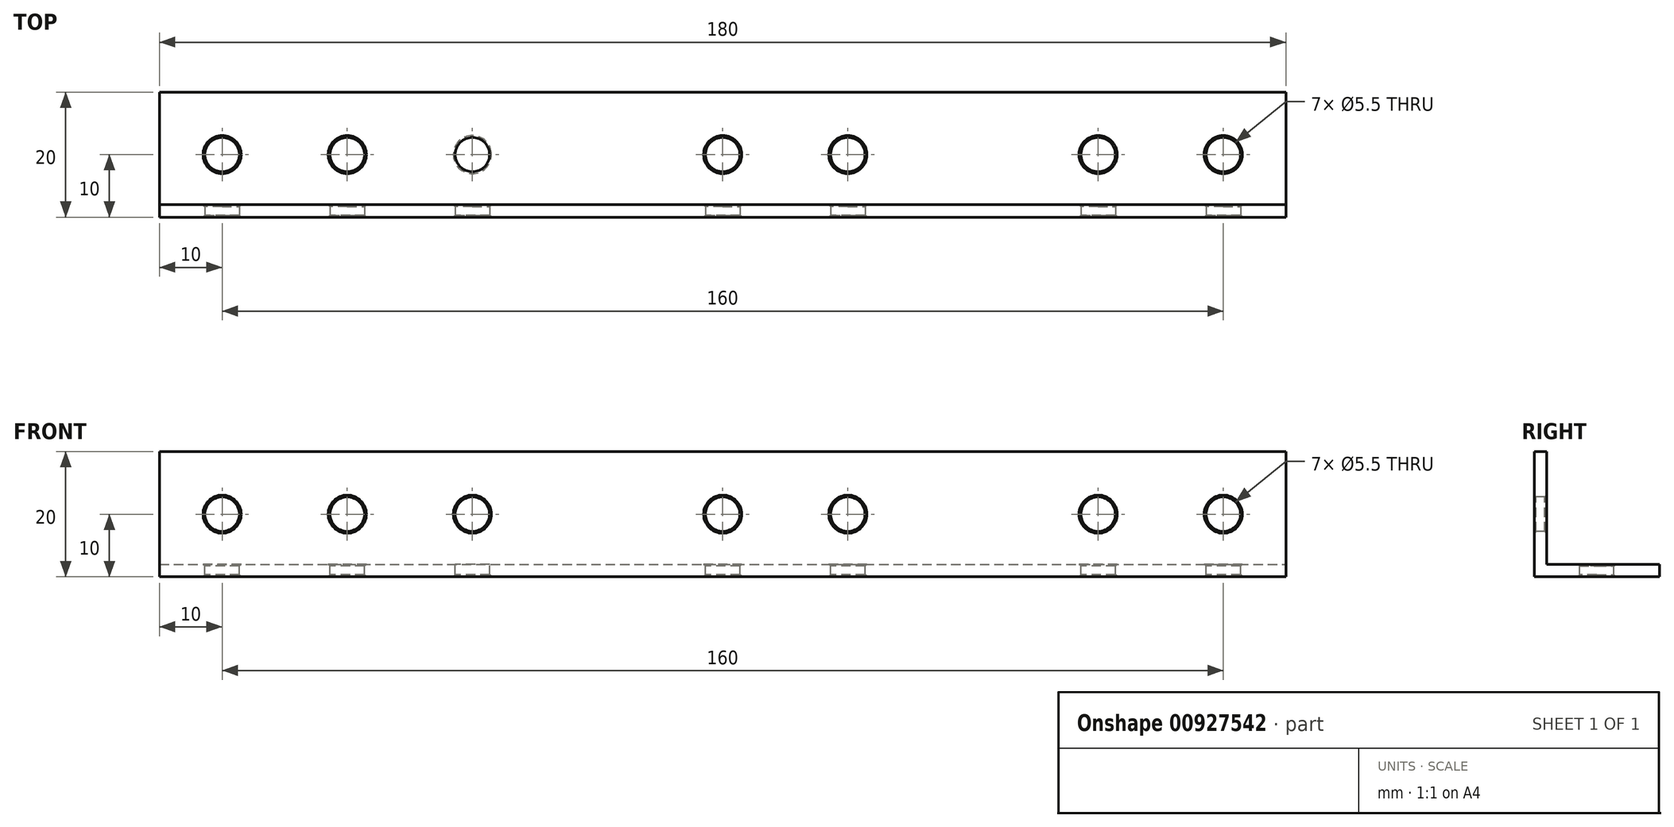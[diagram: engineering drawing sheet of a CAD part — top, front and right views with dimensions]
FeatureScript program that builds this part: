
annotation { "Feature Type Name" : "Feature", "Feature Type Description" : "" }
export const myFeature = defineFeature(function(context is Context, id is Id, definition is map)
    precondition{}
    {
        {
            var Q0;
            Q0=qCreatedBy(makeId("Right.planeOp"),FACE);
            var sketch = newSketch(context, id + "F0", { "sketchPlane" : qUnion([Q0])});
            skLineSegment(sketch, "E0", {"start": v(0, 0) * mm, "end": v(20, 0) * mm});
            skLineSegment(sketch, "E1", {"start": v(20, 0) * mm, "end": v(20, 2) * mm});
            skLineSegment(sketch, "E2", {"start": v(20, 2) * mm, "end": v(2, 2) * mm});
            skLineSegment(sketch, "E3", {"start": v(2, 2) * mm, "end": v(2, 20) * mm});
            skLineSegment(sketch, "E4", {"start": v(2, 20) * mm, "end": v(0, 20) * mm});
            skLineSegment(sketch, "E5", {"start": v(0, 20) * mm, "end": v(0, 0) * mm});
            skSolve(sketch);
        }
        {
            var Q0;
            Q0 = qSketchRegion(id + "F0", true);
            extrude(context, id + "F1", {"entities" : qUnion([Q0]), "oppositeDirection" : true, "depth" : 180 * mm, "offsetDistance" : 25 * mm});
        }
        {
            var Q0;
            Q0=makeQuery(id+"F1.opExtrude","SWEPT_FACE",FACE,{"disambiguationData":[OSD([sQuery(id+"F0.wireOp",EDGE,"E2")])]});
            var sketch = newSketch(context, id + "F2", { "sketchPlane" : qUnion([Q0])});
            skLineSegment(sketch, "E6", {"start": v(-203.4, 10) * mm, "end": v(31.76, 10) * mm, "construction": true});
            skLineSegment(sketch, "E7", {"start": v(-170, 30.5) * mm, "end": v(-170, -11.88) * mm, "construction": true});
            skLineSegment(sketch, "E8", {"start": v(-10, 33.17) * mm, "end": v(-10, -8.91) * mm, "construction": true});
            skCircle(sketch, "E9", {"center": v(-10, 10) * mm, "radius": 2.75 * mm});
            skLineSegment(sketch, "E10", {"start": v(-30, 32.56) * mm, "end": v(-30, -5.19) * mm, "construction": true});
            skLineSegment(sketch, "E11", {"start": v(-70, 34.23) * mm, "end": v(-70, -5.26) * mm, "construction": true});
            skLineSegment(sketch, "E12", {"start": v(-90, 33.62) * mm, "end": v(-90, -7.47) * mm, "construction": true});
            skLineSegment(sketch, "E13", {"start": v(-150, 31.7) * mm, "end": v(-150, -10.96) * mm, "construction": true});
            skCircle(sketch, "E14", {"center": v(-170, 10) * mm, "radius": 2.75 * mm});
            skCircle(sketch, "E15", {"center": v(-150, 10) * mm, "radius": 2.75 * mm});
            skCircle(sketch, "E16", {"center": v(-90, 10) * mm, "radius": 2.75 * mm});
            skCircle(sketch, "E17", {"center": v(-70, 10) * mm, "radius": 2.75 * mm});
            skCircle(sketch, "E18", {"center": v(-30, 10) * mm, "radius": 2.75 * mm});
            skLineSegment(sketch, "E19", {"start": v(-130, 30.56) * mm, "end": v(-130, -11.52) * mm, "construction": true});
            skCircle(sketch, "E20", {"center": v(-130, 10) * mm, "radius": 2.75 * mm});
            skSolve(sketch);
        }
        {
            var Q0;
            Q0 = qSketchRegion(id + "F2", true);
            extrude(context, id + "F3", {"entities" : qUnion([Q0]), "operationType" : NewBodyOperationType.REMOVE, "endBound" : BoundingType.THROUGH_ALL, "oppositeDirection" : true, "depth" : 25 * mm, "offsetDistance" : 25 * mm});
        }
        {
            var Q0;
            Q0=makeQuery(id+"F1.opExtrude","SWEPT_FACE",FACE,{"disambiguationData":[OSD([sQuery(id+"F0.wireOp",EDGE,"E5")])]});
            var sketch = newSketch(context, id + "F4", { "sketchPlane" : qUnion([Q0])});
            skLineSegment(sketch, "E21", {"start": v(-271.94, 10) * mm, "end": v(100.76, 10) * mm, "construction": true});
            skLineSegment(sketch, "E22", {"start": v(-10, 35.8) * mm, "end": v(-10, -12.15) * mm, "construction": true});
            skLineSegment(sketch, "E23", {"start": v(-30, 36.04) * mm, "end": v(-30, -10.38) * mm, "construction": true});
            skLineSegment(sketch, "E24", {"start": v(-70, 30.56) * mm, "end": v(-70, -11.43) * mm, "construction": true});
            skLineSegment(sketch, "E25", {"start": v(-90, 30.4) * mm, "end": v(-90, -9.66) * mm, "construction": true});
            skLineSegment(sketch, "E26", {"start": v(-150, 31.2) * mm, "end": v(-150, -10.06) * mm, "construction": true});
            skLineSegment(sketch, "E27", {"start": v(-170, 31.04) * mm, "end": v(-170, -9.17) * mm, "construction": true});
            skCircle(sketch, "E28", {"center": v(-170, 10) * mm, "radius": 2.75 * mm});
            skCircle(sketch, "E29", {"center": v(-150, 10) * mm, "radius": 2.75 * mm});
            skCircle(sketch, "E30", {"center": v(-90, 10) * mm, "radius": 2.75 * mm});
            skCircle(sketch, "E31", {"center": v(-70, 10) * mm, "radius": 2.75 * mm});
            skCircle(sketch, "E32", {"center": v(-30, 10) * mm, "radius": 2.75 * mm});
            skCircle(sketch, "E33", {"center": v(-10, 10) * mm, "radius": 2.75 * mm});
            skLineSegment(sketch, "E34", {"start": v(-130, 33.32) * mm, "end": v(-130, -20.97) * mm, "construction": true});
            skCircle(sketch, "E35", {"center": v(-130, 10) * mm, "radius": 2.75 * mm});
            skSolve(sketch);
        }
        {
            var Q0;
            Q0 = qSketchRegion(id + "F4", true);
            extrude(context, id + "F5", {"entities" : qUnion([Q0]), "operationType" : NewBodyOperationType.REMOVE, "endBound" : BoundingType.THROUGH_ALL, "oppositeDirection" : true, "depth" : 25 * mm, "offsetDistance" : 25 * mm});
        }
        {
            var Q0;
            Q0=makeQuery(id+"F3.boolean.opBoolean","COPY",FACE,{"derivedFrom":makeQuery(id+"F3.opExtrude","SWEPT_FACE",FACE,{"disambiguationData":[OSD([sQuery(id+"F2.wireOp",EDGE,"E14")])]})});
            var Q1;
            Q1=makeQuery(id+"F3.boolean.opBoolean","COPY",FACE,{"derivedFrom":makeQuery(id+"F3.opExtrude","SWEPT_FACE",FACE,{"disambiguationData":[OSD([sQuery(id+"F2.wireOp",EDGE,"E15")])]})});
            var Q2;
            Q2=makeQuery(id+"F3.boolean.opBoolean","COPY",FACE,{"derivedFrom":makeQuery(id+"F3.opExtrude","SWEPT_FACE",FACE,{"disambiguationData":[OSD([sQuery(id+"F2.wireOp",EDGE,"E16")])]})});
            var Q3;
            Q3=makeQuery(id+"F3.boolean.opBoolean","COPY",FACE,{"derivedFrom":makeQuery(id+"F3.opExtrude","SWEPT_FACE",FACE,{"disambiguationData":[OSD([sQuery(id+"F2.wireOp",EDGE,"E17")])]})});
            var Q4;
            Q4=makeQuery(id+"F3.boolean.opBoolean","COPY",FACE,{"derivedFrom":makeQuery(id+"F3.opExtrude","SWEPT_FACE",FACE,{"disambiguationData":[OSD([sQuery(id+"F2.wireOp",EDGE,"jkiNYSs5-8us3-oUFR-jLsB-93ToUElgCjty")])]})});
            var Q5;
            Q5=makeQuery(id+"F3.boolean.opBoolean","COPY",FACE,{"derivedFrom":makeQuery(id+"F3.opExtrude","SWEPT_FACE",FACE,{"disambiguationData":[OSD([sQuery(id+"F2.wireOp",EDGE,"E18")])]})});
            var Q6;
            Q6=makeQuery(id+"F3.boolean.opBoolean","COPY",FACE,{"derivedFrom":makeQuery(id+"F3.opExtrude","SWEPT_FACE",FACE,{"disambiguationData":[OSD([sQuery(id+"F2.wireOp",EDGE,"E9")])]})});
            var Q7;
            Q7=makeQuery(id+"F5.boolean.opBoolean","COPY",FACE,{"derivedFrom":makeQuery(id+"F5.opExtrude","SWEPT_FACE",FACE,{"disambiguationData":[OSD([sQuery(id+"F4.wireOp",EDGE,"E33")])]})});
            var Q8;
            Q8=makeQuery(id+"F5.boolean.opBoolean","COPY",FACE,{"derivedFrom":makeQuery(id+"F5.opExtrude","SWEPT_FACE",FACE,{"disambiguationData":[OSD([sQuery(id+"F4.wireOp",EDGE,"E32")])]})});
            var Q9;
            Q9=makeQuery(id+"F5.boolean.opBoolean","COPY",FACE,{"derivedFrom":makeQuery(id+"F5.opExtrude","SWEPT_FACE",FACE,{"disambiguationData":[OSD([sQuery(id+"F4.wireOp",EDGE,"yGnBm6ms-4C5B-GAF8-uEHt-rKr5TpWDp7Mf")])]})});
            var Q10;
            Q10=makeQuery(id+"F5.boolean.opBoolean","COPY",FACE,{"derivedFrom":makeQuery(id+"F5.opExtrude","SWEPT_FACE",FACE,{"disambiguationData":[OSD([sQuery(id+"F4.wireOp",EDGE,"E31")])]})});
            var Q11;
            Q11=makeQuery(id+"F5.boolean.opBoolean","COPY",FACE,{"derivedFrom":makeQuery(id+"F5.opExtrude","SWEPT_FACE",FACE,{"disambiguationData":[OSD([sQuery(id+"F4.wireOp",EDGE,"E30")])]})});
            var Q12;
            Q12=makeQuery(id+"F5.boolean.opBoolean","COPY",FACE,{"derivedFrom":makeQuery(id+"F5.opExtrude","SWEPT_FACE",FACE,{"disambiguationData":[OSD([sQuery(id+"F4.wireOp",EDGE,"E29")])]})});
            var Q13;
            Q13=makeQuery(id+"F5.boolean.opBoolean","COPY",FACE,{"derivedFrom":makeQuery(id+"F5.opExtrude","SWEPT_FACE",FACE,{"disambiguationData":[OSD([sQuery(id+"F4.wireOp",EDGE,"E28")])]})});
            var Q14;
            Q14=makeQuery(id+"F3.boolean.opBoolean","INTERSECT",EDGE,{"derivedFrom":[makeQuery(id+"F1.opExtrude","SWEPT_FACE",FACE,{"disambiguationData":[OSD([sQuery(id+"F0.wireOp",EDGE,"E0")])]}),makeQuery(id+"F3.opExtrude","SWEPT_FACE",FACE,{"disambiguationData":[OSD([sQuery(id+"F2.wireOp",EDGE,"E20")])]})]});
            var Q15;
            Q15=makeQuery(id+"F3.boolean.opBoolean","COPY",EDGE,{"derivedFrom":makeQuery(id+"F3.opExtrude","CAP_EDGE",EDGE,{"disambiguationData":[OSD([sQuery(id+"F2.wireOp",EDGE,"E20")])],"isStart":true})});
            var Q16;
            Q16=makeQuery(id+"F5.boolean.opBoolean","COPY",FACE,{"derivedFrom":makeQuery(id+"F5.opExtrude","SWEPT_FACE",FACE,{"disambiguationData":[OSD([sQuery(id+"F4.wireOp",EDGE,"E35")])]})});
            chamfer(context, id + "F6", {"entities" : qUnion([Q0, Q1, Q2, Q3, Q4, Q5, Q6, Q7, Q8, Q9, Q10, Q11, Q12, Q13, Q14, Q15, Q16]), "width" : 0.3 * mm, "tangentPropagation" : true});
        }
    });
